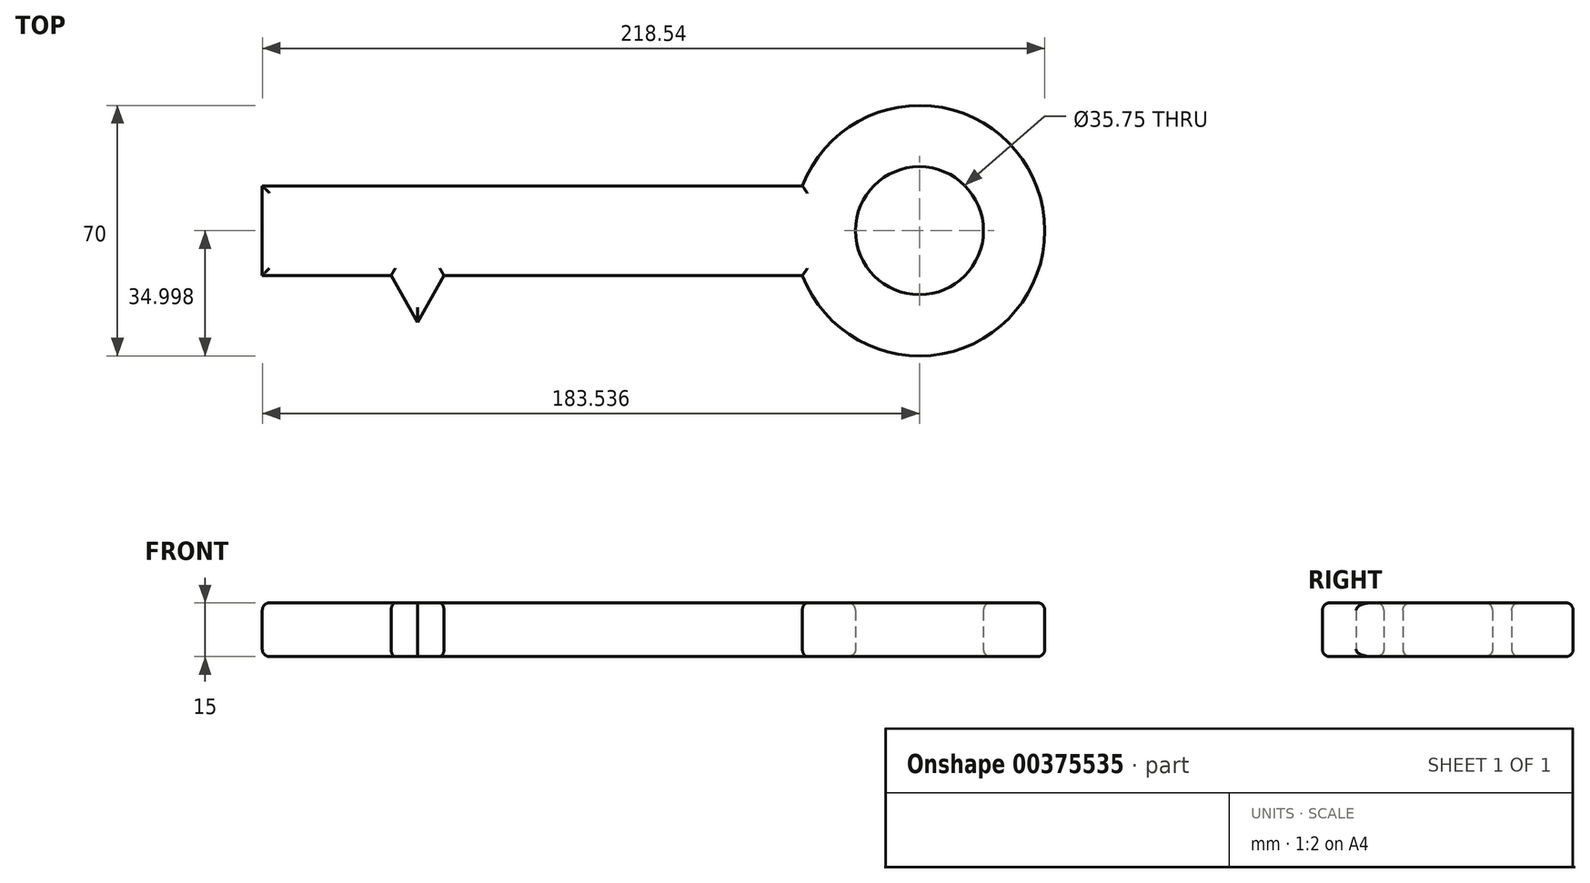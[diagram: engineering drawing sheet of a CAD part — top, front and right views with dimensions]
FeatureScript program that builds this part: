
annotation { "Feature Type Name" : "Feature", "Feature Type Description" : "" }
export const myFeature = defineFeature(function(context is Context, id is Id, definition is map)
    precondition{}
    {
        {
            var Q0;
            Q0=qCreatedBy(makeId("Top.planeOp"),FACE);
            var sketch = newSketch(context, id + "F0", { "sketchPlane" : qUnion([Q0])});
            skLineSegment(sketch, "E0.bottom", {"start": v(-41.27, 26.84) * mm, "end": v(109.57, 26.84) * mm});
            skLineSegment(sketch, "E0.top", {"start": v(-41.27, 1.84) * mm, "end": v(109.57, 1.84) * mm});
            skLineSegment(sketch, "E0.left", {"start": v(-41.27, 26.84) * mm, "end": v(-41.27, 1.84) * mm});
            skLineSegment(sketch, "E0.right", {"start": v(109.57, 26.84) * mm, "end": v(109.57, 1.84) * mm});
            skLineSegment(sketch, "E1.bottom", {"start": v(-41.27, 1.84) * mm, "end": v(-33.27, 1.84) * mm});
            skLineSegment(sketch, "E1.top", {"start": v(-41.27, -28.16) * mm, "end": v(-33.27, -28.16) * mm});
            skLineSegment(sketch, "E1.left", {"start": v(-41.27, 1.84) * mm, "end": v(-41.27, -28.16) * mm});
            skLineSegment(sketch, "E1.right", {"start": v(-33.27, 1.84) * mm, "end": v(-33.27, -28.16) * mm});
            skLineSegment(sketch, "E2.bottom", {"start": v(-23.27, 1.84) * mm, "end": v(-15.27, 1.84) * mm});
            skLineSegment(sketch, "E2.top", {"start": v(-23.27, -13.16) * mm, "end": v(-15.27, -13.16) * mm});
            skLineSegment(sketch, "E2.left", {"start": v(-23.27, 1.84) * mm, "end": v(-23.27, -13.16) * mm});
            skLineSegment(sketch, "E2.right", {"start": v(-15.27, 1.84) * mm, "end": v(-15.27, -13.16) * mm});
            skLineSegment(sketch, "E3", {"start": v(-5.27, 1.84) * mm, "end": v(2.1, -11.23) * mm});
            skLineSegment(sketch, "E4", {"start": v(2.1, -11.23) * mm, "end": v(9.45, 1.84) * mm});
            skArc(sketch, "E5", {"start": v(109.57, 1.84) * mm, "mid": v(177.27, 14.34) * mm, "end": v(109.57, 26.84) * mm});
            skCircle(sketch, "E6", {"center": v(142.27, 14.34) * mm, "radius": 17.87 * mm});
            skLineSegment(sketch, "E7", {"start": v(-41.27, 14.34) * mm, "end": v(142.27, 14.34) * mm, "construction": true});
            skSolve(sketch);
        }
        {
            var Q0;
            {var subQ0=sQuery(id+"F0.wireOp",EDGE,"E3");Q0=makeQuery(id+"F0.imprint","IMPRINT",FACE,{"disambiguationData":[TD([[makeQuery(id+"F0.imprint","IMPRINT",EDGE,{"derivedFrom":subQ0}),1.0]])]});}
            var Q1;
            Q1=makeQuery(id+"F0.imprint","IMPRINT",FACE,{"disambiguationData":[TD([[makeQuery(id+"F0.imprint","IMPRINT",EDGE,{"derivedFrom":sQuery(id+"F0.wireOp",EDGE,"E1.bottom")}),-1.0]])]});
            var Q2;
            Q2=makeQuery(id+"F0.imprint","IMPRINT",FACE,{"disambiguationData":[TD([[makeQuery(id+"F0.imprint","IMPRINT",EDGE,{"derivedFrom":sQuery(id+"F0.wireOp",EDGE,"E2.bottom")}),-1.0]])]});
            var Q3;
            Q3=makeQuery(id+"F0.imprint","IMPRINT",FACE,{"disambiguationData":[TD([[makeQuery(id+"F0.imprint","IMPRINT",EDGE,{"derivedFrom":sQuery(id+"F0.wireOp",EDGE,"E0.right")}),1.0]])]});
            var Q4;
            Q4=makeQuery(id+"F0.imprint","IMPRINT",FACE,{"disambiguationData":[TD([[makeQuery(id+"F0.imprint","IMPRINT",EDGE,{"derivedFrom":sQuery(id+"F0.wireOp",EDGE,"E0.bottom")}),-1.0]])]});
            extrude(context, id + "F1", {"entities" : qUnion([Q0, Q1, Q2, Q3, Q4]), "depth" : 15 * mm});
        }
        {
            var Q0;
            Q0=makeQuery(id+"F1.opExtrude","CAP_FACE",FACE,{"disambiguationData":[OSD([sQuery(id+"F0.wireOp",EDGE,"E0.bottom"),sQuery(id+"F0.wireOp",EDGE,"E0.top"),sQuery(id+"F0.wireOp",EDGE,"E0.left"),sQuery(id+"F0.wireOp",EDGE,"E1.top"),sQuery(id+"F0.wireOp",EDGE,"E1.left"),sQuery(id+"F0.wireOp",EDGE,"E1.right"),sQuery(id+"F0.wireOp",EDGE,"E2.top"),sQuery(id+"F0.wireOp",EDGE,"E2.left"),sQuery(id+"F0.wireOp",EDGE,"E2.right"),sQuery(id+"F0.wireOp",EDGE,"E3"),sQuery(id+"F0.wireOp",EDGE,"E4"),sQuery(id+"F0.wireOp",EDGE,"E5"),sQuery(id+"F0.wireOp",EDGE,"E6")])],"isStart":false});
            var Q1;
            Q1=makeQuery(id+"F1.opExtrude","CAP_FACE",FACE,{"disambiguationData":[OSD([sQuery(id+"F0.wireOp",EDGE,"E0.bottom"),sQuery(id+"F0.wireOp",EDGE,"E0.top"),sQuery(id+"F0.wireOp",EDGE,"E0.left"),sQuery(id+"F0.wireOp",EDGE,"E1.top"),sQuery(id+"F0.wireOp",EDGE,"E1.left"),sQuery(id+"F0.wireOp",EDGE,"E1.right"),sQuery(id+"F0.wireOp",EDGE,"E2.top"),sQuery(id+"F0.wireOp",EDGE,"E2.left"),sQuery(id+"F0.wireOp",EDGE,"E2.right"),sQuery(id+"F0.wireOp",EDGE,"E3"),sQuery(id+"F0.wireOp",EDGE,"E4"),sQuery(id+"F0.wireOp",EDGE,"E5"),sQuery(id+"F0.wireOp",EDGE,"E6")])],"isStart":true});
            fillet(context, id + "F2", {"entities" : qUnion([Q0, Q1]), "radius" : 2 * mm, "tangentPropagation" : true, "allowEdgeOverflow" : false});
        }
    });
